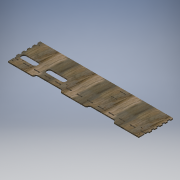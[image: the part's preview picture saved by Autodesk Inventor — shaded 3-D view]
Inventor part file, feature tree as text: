
AUTODESK INVENTOR PART (.ipt)
format: ipt  version: 2018.3 (Build 223284000, 284)  size: 4,857,856 bytes
history: native  units: mm
features: reference x20, other x8, extrude x5, sketch x5
ambient origin geometry x8: Origin, YZ Plane, XZ Plane, XY Plane, X Axis, Y Axis, Z Axis, Center Point
bodies: Solido1 (feature_tree)
feature tree (38):
  extrude  "Estrusione1"  Depth=95.0mm
  extrude  "Estrusione2"  TaperAngle=90.0deg  [1 undecoded]
  extrude  "Estrusione3"  Depth=95.0mm
  extrude  "Estrusione4"  Depth=5.0mm
  extrude  "Estrusione5"  Depth=90.0mm
  sketch  "Schizzo1"
  reference  "Riferimento1"
  reference  "Riferimento2"
  reference  "Riferimento3"
  reference  "Riferimento4"
  reference  "Riferimento5"
  reference  "Riferimento6"
  reference  "Riferimento7"
  reference  "Riferimento8"
  reference  "Riferimento9"
  reference  "Riferimento10"
  reference  "Riferimento11"
  reference  "Riferimento12"
  reference  "Riferimento13"
  sketch  "Schizzo2"
  reference  "Riferimento14"
  reference  "Riferimento15"
  reference  "Riferimento16"
  reference  "Riferimento17"
  sketch  "Schizzo3"
  reference  "Riferimento18"
  reference  "Riferimento19"
  reference  "Riferimento20"
  sketch  "Schizzo5"
  other  "Linea chiusa proiettata1"
  sketch  "Schizzo6"
  other  "Immagine2"
  other  "Immagine3"
  other  "<userpath>\Desktop\Scorbot Hardware\Case Board\caseHw.iam"
  other  "caseHw.iam"
  other  "tavolaBase:1"
  other  "LatoAlimentatore:1"
  other  "LatoPy:1"
note: 1 required parameter value undecoded (feature->parameter linkage not recoverable at this tier; creation-order binding heuristic only, values carry confidence <= 0.55)
